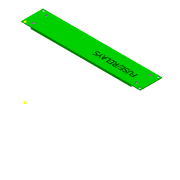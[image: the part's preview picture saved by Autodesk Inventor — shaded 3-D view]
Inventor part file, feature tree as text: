
AUTODESK INVENTOR PART (.ipt)
format: ipt  version: 2016 SP2 (Build 200236200, 236)  size: 159,232 bytes
history: native  units: mm
features: sketch x2
ambient origin geometry x8: Origin, YZ Plane, XZ Plane, XY Plane, X Axis, Y Axis, Z Axis, Center Point
bodies: Solid1 (feature_tree)
feature tree (2):
  sketch  "Sketch1"
  sketch  "Sketch2"
